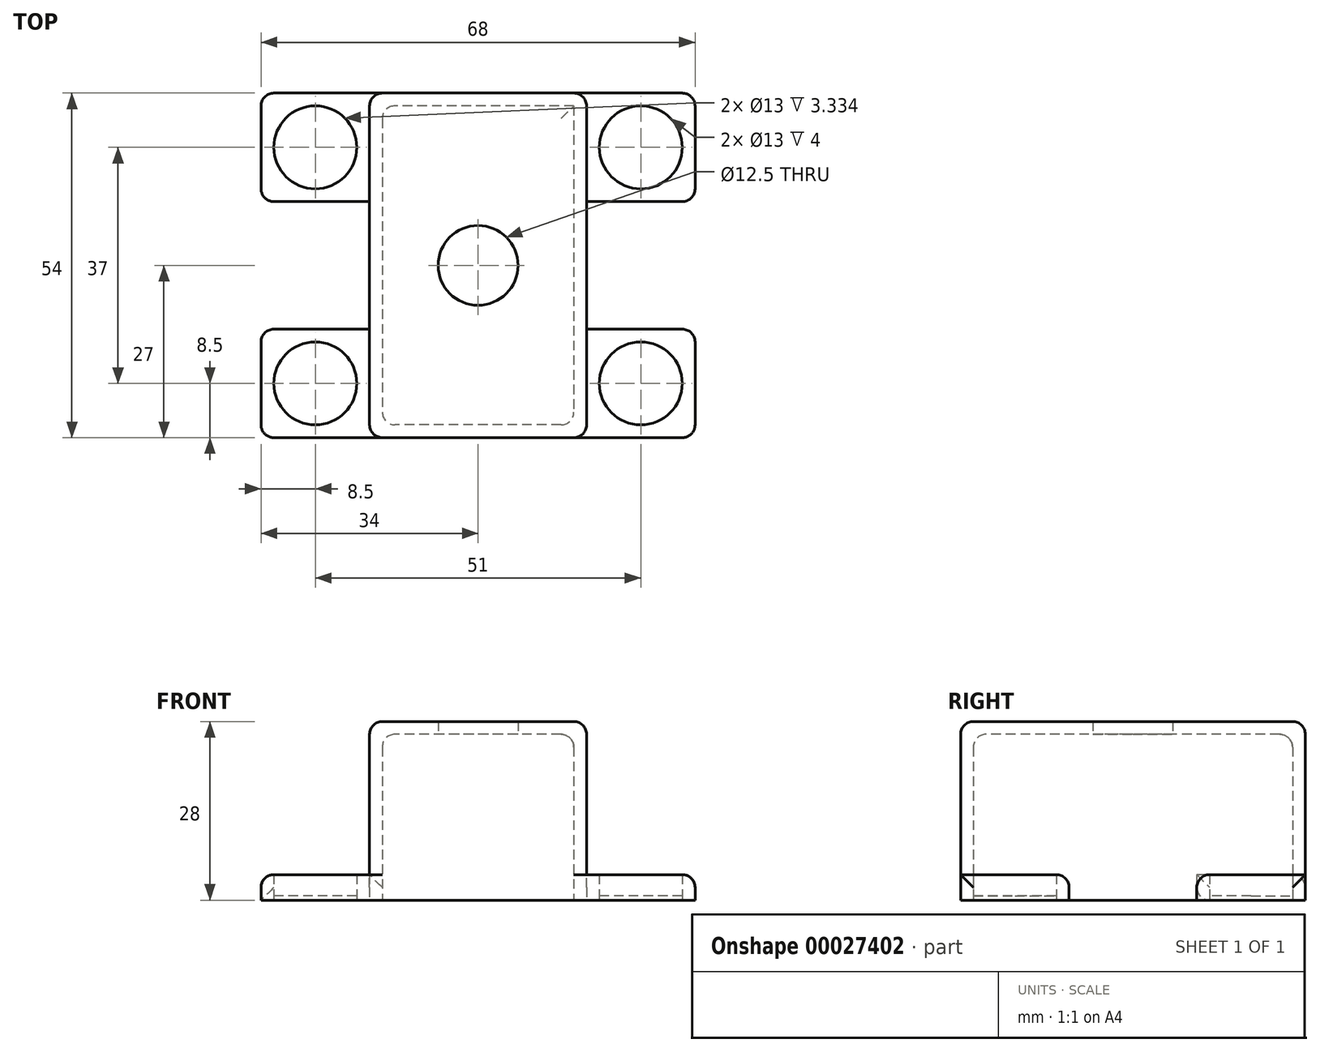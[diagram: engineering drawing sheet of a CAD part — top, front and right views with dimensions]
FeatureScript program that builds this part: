
annotation { "Feature Type Name" : "Feature", "Feature Type Description" : "" }
export const myFeature = defineFeature(function(context is Context, id is Id, definition is map)
    precondition{}
    {
        {
            var Q0;
            Q0=qCreatedBy(makeId("Top.planeOp"),FACE);
            var sketch = newSketch(context, id + "F0", { "sketchPlane" : qUnion([Q0])});
            skLineSegment(sketch, "E0.rect.bottom", {"start": v(17, 27) * mm, "end": v(-17, 27) * mm});
            skLineSegment(sketch, "E0.rect.top", {"start": v(17, -27) * mm, "end": v(-17, -27) * mm});
            skLineSegment(sketch, "E0.rect.left", {"start": v(17, 27) * mm, "end": v(17, -27) * mm});
            skLineSegment(sketch, "E0.rect.right", {"start": v(-17, 27) * mm, "end": v(-17, -27) * mm});
            skPoint(sketch, "E0.rect.middle", {"position": v(0, 0) * mm});
            skLineSegment(sketch, "E1", {"start": v(0, -27) * mm, "end": v(0, 27) * mm, "construction": true});
            skCircle(sketch, "E2", {"center": v(0, 0) * mm, "radius": 6.25 * mm});
            skLineSegment(sketch, "E3.0", {"start": v(-15, 25) * mm, "end": v(-15, -25) * mm});
            skLineSegment(sketch, "E3.1", {"start": v(15, 25) * mm, "end": v(-15, 25) * mm});
            skLineSegment(sketch, "E3.2", {"start": v(15, 25) * mm, "end": v(15, -25) * mm});
            skLineSegment(sketch, "E3.3", {"start": v(15, -25) * mm, "end": v(-15, -25) * mm});
            skCircle(sketch, "E4", {"center": v(-25.5, 18.5) * mm, "radius": 6.5 * mm});
            skLineSegment(sketch, "E5", {"start": v(-17, 27) * mm, "end": v(-34, 27) * mm});
            skLineSegment(sketch, "E6", {"start": v(-34, 27) * mm, "end": v(-34, 10) * mm});
            skLineSegment(sketch, "E7", {"start": v(-34, 10) * mm, "end": v(-17, 10) * mm});
            skLineSegment(sketch, "E8.MirrorCS", {"start": v(34, 10) * mm, "end": v(17, 10) * mm});
            skCircle(sketch, "E9.MirrorC", {"center": v(25.5, 18.5) * mm, "radius": 6.5 * mm});
            skLineSegment(sketch, "E10.MirrorCS", {"start": v(34, 27) * mm, "end": v(34, 10) * mm});
            skLineSegment(sketch, "E11.MirrorCS", {"start": v(17, 27) * mm, "end": v(34, 27) * mm});
            skLineSegment(sketch, "E12", {"start": v(-17, 0) * mm, "end": v(17, 0) * mm, "construction": true});
            skCircle(sketch, "E13.MirrorC", {"center": v(25.5, -18.5) * mm, "radius": 6.5 * mm});
            skLineSegment(sketch, "E14.MirrorCS", {"start": v(34, -27) * mm, "end": v(34, -10) * mm});
            skLineSegment(sketch, "E15.MirrorCS", {"start": v(17, -27) * mm, "end": v(34, -27) * mm});
            skLineSegment(sketch, "E16.MirrorCS", {"start": v(34, -10) * mm, "end": v(17, -10) * mm});
            skLineSegment(sketch, "E17.MirrorCS", {"start": v(-34, -10) * mm, "end": v(-17, -10) * mm});
            skLineSegment(sketch, "E18.MirrorCS", {"start": v(-34, -27) * mm, "end": v(-34, -10) * mm});
            skLineSegment(sketch, "E19.MirrorCS", {"start": v(-17, -27) * mm, "end": v(-34, -27) * mm});
            skCircle(sketch, "E20.MirrorC", {"center": v(-25.5, -18.5) * mm, "radius": 6.5 * mm});
            skSolve(sketch);
        }
        {
            var Q0;
            {var subQ4=sQuery(id+"F0.wireOp",EDGE,"E0.rect.bottom");Q0=makeQuery(id+"F0.imprint","IMPRINT",FACE,{"disambiguationData":[TD([[makeQuery(id+"F0.imprint","IMPRINT",EDGE,{"derivedFrom":subQ4}),1.0]])]});}
            var Q1;
            Q1=makeQuery(id+"F0.imprint","IMPRINT",FACE,{"disambiguationData":[TD([[makeQuery(id+"F0.imprint","IMPRINT",EDGE,{"derivedFrom":sQuery(id+"F0.wireOp",EDGE,"E2")}),1.0]])]});
            var Q2;
            Q2=makeQuery(id+"F0.imprint","IMPRINT",FACE,{"disambiguationData":[TD([[makeQuery(id+"F0.imprint","IMPRINT",EDGE,{"derivedFrom":sQuery(id+"F0.wireOp",EDGE,"E2")}),-1.0]])]});
            extrude(context, id + "F1", {"entities" : qUnion([Q0, Q1, Q2]), "depth" : 28 * mm});
        }
        {
            var Q0;
            Q0=makeQuery(id+"F0.imprint","IMPRINT",FACE,{"disambiguationData":[TD([[makeQuery(id+"F0.imprint","IMPRINT",EDGE,{"derivedFrom":sQuery(id+"F0.wireOp",EDGE,"E2")}),1.0]])]});
            extrude(context, id + "F2", {"entities" : qUnion([Q0]), "operationType" : NewBodyOperationType.REMOVE, "endBound" : BoundingType.THROUGH_ALL, "depth" : 25 * mm});
        }
        {
            var Q0;
            Q0=makeQuery(id+"F0.imprint","IMPRINT",FACE,{"disambiguationData":[TD([[makeQuery(id+"F0.imprint","IMPRINT",EDGE,{"derivedFrom":sQuery(id+"F0.wireOp",EDGE,"E2")}),-1.0]])]});
            extrude(context, id + "F3", {"entities" : qUnion([Q0]), "operationType" : NewBodyOperationType.REMOVE, "depth" : 26 * mm});
        }
        {
            var Q0;
            Q0=makeQuery(id+"F0.imprint","IMPRINT",FACE,{"disambiguationData":[TD([[makeQuery(id+"F0.imprint","IMPRINT",EDGE,{"derivedFrom":sQuery(id+"F0.wireOp",EDGE,"E4")}),-1.0]])]});
            var Q1;
            {var subQ1=sQuery(id+"F0.wireOp",EDGE,"E8.MirrorCS");Q1=makeQuery(id+"F0.imprint","IMPRINT",FACE,{"disambiguationData":[TD([[makeQuery(id+"F0.imprint","IMPRINT",EDGE,{"derivedFrom":subQ1}),-1.0]])]});}
            var Q2;
            Q2=makeQuery(id+"F0.imprint","IMPRINT",FACE,{"disambiguationData":[TD([[makeQuery(id+"F0.imprint","IMPRINT",EDGE,{"derivedFrom":sQuery(id+"F0.wireOp",EDGE,"E13.MirrorC")}),-1.0]])]});
            var Q3;
            {var subQ1=sQuery(id+"F0.wireOp",EDGE,"E17.MirrorCS");Q3=makeQuery(id+"F0.imprint","IMPRINT",FACE,{"disambiguationData":[TD([[makeQuery(id+"F0.imprint","IMPRINT",EDGE,{"derivedFrom":subQ1}),-1.0]])]});}
            extrude(context, id + "F4", {"entities" : qUnion([Q0, Q1, Q2, Q3]), "operationType" : NewBodyOperationType.ADD, "depth" : 4 * mm});
        }
        {
            var Q0;
            Q0=makeQuery(id+"F0.imprint","IMPRINT",FACE,{"disambiguationData":[TD([[makeQuery(id+"F0.imprint","IMPRINT",EDGE,{"derivedFrom":sQuery(id+"F0.wireOp",EDGE,"E9.MirrorC")}),-1.0]])]});
            var Q1;
            Q1=makeQuery(id+"F0.imprint","IMPRINT",FACE,{"disambiguationData":[TD([[makeQuery(id+"F0.imprint","IMPRINT",EDGE,{"derivedFrom":sQuery(id+"F0.wireOp",EDGE,"E13.MirrorC")}),1.0]])]});
            var Q2;
            Q2=makeQuery(id+"F0.imprint","IMPRINT",FACE,{"disambiguationData":[TD([[makeQuery(id+"F0.imprint","IMPRINT",EDGE,{"derivedFrom":sQuery(id+"F0.wireOp",EDGE,"E20.MirrorC")}),-1.0]])]});
            var Q3;
            Q3=makeQuery(id+"F0.imprint","IMPRINT",FACE,{"disambiguationData":[TD([[makeQuery(id+"F0.imprint","IMPRINT",EDGE,{"derivedFrom":sQuery(id+"F0.wireOp",EDGE,"E4")}),1.0]])]});
            extrude(context, id + "F5", {"entities" : qUnion([Q0, Q1, Q2, Q3]), "operationType" : NewBodyOperationType.ADD, "depth" : .666 * mm});
        }
        {
            var Q0;
            Q0=makeQuery(id+"F4.opExtrude","SWEPT_EDGE",EDGE,{"disambiguationData":[OSD([sQuery(id+"F0.wireOp",EDGE,"E18.MirrorCS"),sQuery(id+"F0.wireOp",EDGE,"E19.MirrorCS")])]});
            var Q1;
            Q1=makeQuery(id+"F4.opExtrude","SWEPT_EDGE",EDGE,{"disambiguationData":[OSD([sQuery(id+"F0.wireOp",EDGE,"E17.MirrorCS"),sQuery(id+"F0.wireOp",EDGE,"E18.MirrorCS")])]});
            var Q2;
            {var subQ0=sQuery(id+"F0.wireOp",EDGE,"E0.rect.right");Q2=makeQuery(id+"F4.opExtrude","CAP_EDGE",EDGE,{"disambiguationData":[OSD([subQ0]),TDD([makeQuery(id+"F0.imprint","IMPRINT",EDGE,{"disambiguationData":[TD([[makeQuery(id+"F0.imprint","INTERSECT",VERTEX,{"derivedFrom":[subQ0,sQuery(id+"F0.wireOp",EDGE,"E17.MirrorCS")]}),-1.0]])],"derivedFrom":subQ0})])],"isStart":false});}
            var Q3;
            Q3=makeQuery(id+"F4.opExtrude","SWEPT_EDGE",EDGE,{"disambiguationData":[OSD([sQuery(id+"F0.wireOp",EDGE,"E0.rect.right"),sQuery(id+"F0.wireOp",EDGE,"E17.MirrorCS")])]});
            var Q4;
            Q4=makeQuery(id+"F4.opExtrude","SWEPT_EDGE",EDGE,{"disambiguationData":[OSD([sQuery(id+"F0.wireOp",EDGE,"E0.rect.right"),sQuery(id+"F0.wireOp",EDGE,"E7")])]});
            var Q5;
            Q5=makeQuery(id+"F4.opExtrude","SWEPT_EDGE",EDGE,{"disambiguationData":[OSD([sQuery(id+"F0.wireOp",EDGE,"E6"),sQuery(id+"F0.wireOp",EDGE,"E7")])]});
            var Q6;
            Q6=makeQuery(id+"F4.opExtrude","SWEPT_EDGE",EDGE,{"disambiguationData":[OSD([sQuery(id+"F0.wireOp",EDGE,"E5"),sQuery(id+"F0.wireOp",EDGE,"E6")])]});
            var Q7;
            {var subQ0=sQuery(id+"F0.wireOp",EDGE,"E0.rect.right");Q7=makeQuery(id+"F4.opExtrude","CAP_EDGE",EDGE,{"disambiguationData":[OSD([subQ0]),TDD([makeQuery(id+"F0.imprint","IMPRINT",EDGE,{"disambiguationData":[TD([[makeQuery(id+"F0.imprint","INTERSECT",VERTEX,{"derivedFrom":[subQ0,sQuery(id+"F0.wireOp",EDGE,"E7")]}),1.0]])],"derivedFrom":subQ0})])],"isStart":false});}
            var Q8;
            Q8=makeQuery(id+"F4.opExtrude","SWEPT_EDGE",EDGE,{"disambiguationData":[OSD([sQuery(id+"F0.wireOp",EDGE,"E0.rect.left"),sQuery(id+"F0.wireOp",EDGE,"E8.MirrorCS")])]});
            var Q9;
            {var subQ0=sQuery(id+"F0.wireOp",EDGE,"E0.rect.left");Q9=makeQuery(id+"F4.opExtrude","CAP_EDGE",EDGE,{"disambiguationData":[OSD([subQ0]),TDD([makeQuery(id+"F0.imprint","IMPRINT",EDGE,{"disambiguationData":[TD([[makeQuery(id+"F0.imprint","INTERSECT",VERTEX,{"derivedFrom":[subQ0,sQuery(id+"F0.wireOp",EDGE,"E8.MirrorCS")]}),1.0]])],"derivedFrom":subQ0})])],"isStart":false});}
            var Q10;
            Q10=makeQuery(id+"F4.opExtrude","SWEPT_EDGE",EDGE,{"disambiguationData":[OSD([sQuery(id+"F0.wireOp",EDGE,"E8.MirrorCS"),sQuery(id+"F0.wireOp",EDGE,"E10.MirrorCS")])]});
            var Q11;
            Q11=makeQuery(id+"F4.opExtrude","SWEPT_EDGE",EDGE,{"disambiguationData":[OSD([sQuery(id+"F0.wireOp",EDGE,"E10.MirrorCS"),sQuery(id+"F0.wireOp",EDGE,"E11.MirrorCS")])]});
            var Q12;
            Q12=makeQuery(id+"F4.opExtrude","SWEPT_EDGE",EDGE,{"disambiguationData":[OSD([sQuery(id+"F0.wireOp",EDGE,"E14.MirrorCS"),sQuery(id+"F0.wireOp",EDGE,"E16.MirrorCS")])]});
            var Q13;
            {var subQ0=sQuery(id+"F0.wireOp",EDGE,"E0.rect.left");Q13=makeQuery(id+"F4.opExtrude","CAP_EDGE",EDGE,{"disambiguationData":[OSD([subQ0]),TDD([makeQuery(id+"F0.imprint","IMPRINT",EDGE,{"disambiguationData":[TD([[makeQuery(id+"F0.imprint","INTERSECT",VERTEX,{"derivedFrom":[subQ0,sQuery(id+"F0.wireOp",EDGE,"E16.MirrorCS")]}),-1.0]])],"derivedFrom":subQ0})])],"isStart":false});}
            var Q14;
            Q14=makeQuery(id+"F4.opExtrude","SWEPT_EDGE",EDGE,{"disambiguationData":[OSD([sQuery(id+"F0.wireOp",EDGE,"E14.MirrorCS"),sQuery(id+"F0.wireOp",EDGE,"E15.MirrorCS")])]});
            var Q15;
            Q15=makeQuery(id+"F4.opExtrude","SWEPT_EDGE",EDGE,{"disambiguationData":[OSD([sQuery(id+"F0.wireOp",EDGE,"E0.rect.left"),sQuery(id+"F0.wireOp",EDGE,"E16.MirrorCS")])]});
            var Q16;
            Q16=makeQuery(id+"F1.opExtrude","SWEPT_EDGE",EDGE,{"disambiguationData":[OSD([sQuery(id+"F0.wireOp",EDGE,"E0.rect.bottom"),sQuery(id+"F0.wireOp",EDGE,"E0.rect.left"),sQuery(id+"F0.wireOp",EDGE,"E11.MirrorCS")])]});
            var Q17;
            Q17=makeQuery(id+"F4.opExtrude","CAP_EDGE",EDGE,{"disambiguationData":[OSD([sQuery(id+"F0.wireOp",EDGE,"E10.MirrorCS")])],"isStart":false});
            var Q18;
            Q18=makeQuery(id+"F4.opExtrude","CAP_EDGE",EDGE,{"disambiguationData":[OSD([sQuery(id+"F0.wireOp",EDGE,"E8.MirrorCS")])],"isStart":false});
            var Q19;
            Q19=makeQuery(id+"F1.opExtrude","SWEPT_EDGE",EDGE,{"disambiguationData":[OSD([sQuery(id+"F0.wireOp",EDGE,"E0.rect.bottom"),sQuery(id+"F0.wireOp",EDGE,"E0.rect.right"),sQuery(id+"F0.wireOp",EDGE,"E5")])]});
            var Q20;
            Q20=makeQuery(id+"F4.opExtrude","CAP_EDGE",EDGE,{"disambiguationData":[OSD([sQuery(id+"F0.wireOp",EDGE,"E5")])],"isStart":false});
            var Q21;
            Q21=makeQuery(id+"F4.opExtrude","CAP_EDGE",EDGE,{"disambiguationData":[OSD([sQuery(id+"F0.wireOp",EDGE,"E6")])],"isStart":false});
            var Q22;
            Q22=makeQuery(id+"F4.opExtrude","CAP_EDGE",EDGE,{"disambiguationData":[OSD([sQuery(id+"F0.wireOp",EDGE,"E7")])],"isStart":true});
            var Q23;
            Q23=makeQuery(id+"F1.opExtrude","SWEPT_EDGE",EDGE,{"disambiguationData":[OSD([sQuery(id+"F0.wireOp",EDGE,"E0.rect.top"),sQuery(id+"F0.wireOp",EDGE,"E0.rect.right"),sQuery(id+"F0.wireOp",EDGE,"E19.MirrorCS")])]});
            var Q24;
            Q24=makeQuery(id+"F4.opExtrude","CAP_EDGE",EDGE,{"disambiguationData":[OSD([sQuery(id+"F0.wireOp",EDGE,"E18.MirrorCS")])],"isStart":false});
            var Q25;
            Q25=makeQuery(id+"F4.opExtrude","CAP_EDGE",EDGE,{"disambiguationData":[OSD([sQuery(id+"F0.wireOp",EDGE,"E17.MirrorCS")])],"isStart":false});
            var Q26;
            Q26=makeQuery(id+"F1.opExtrude","SWEPT_EDGE",EDGE,{"disambiguationData":[OSD([sQuery(id+"F0.wireOp",EDGE,"E0.rect.top"),sQuery(id+"F0.wireOp",EDGE,"E0.rect.left"),sQuery(id+"F0.wireOp",EDGE,"E15.MirrorCS")])]});
            var Q27;
            Q27=makeQuery(id+"F4.opExtrude","CAP_EDGE",EDGE,{"disambiguationData":[OSD([sQuery(id+"F0.wireOp",EDGE,"E14.MirrorCS")])],"isStart":false});
            var Q28;
            Q28=makeQuery(id+"F4.opExtrude","CAP_EDGE",EDGE,{"disambiguationData":[OSD([sQuery(id+"F0.wireOp",EDGE,"E16.MirrorCS")])],"isStart":false});
            var Q29;
            Q29=makeQuery(id+"F1.opExtrude","CAP_EDGE",EDGE,{"disambiguationData":[OSD([sQuery(id+"F0.wireOp",EDGE,"E0.rect.left")])],"isStart":false});
            var Q30;
            Q30=makeQuery(id+"F1.opExtrude","CAP_EDGE",EDGE,{"disambiguationData":[OSD([sQuery(id+"F0.wireOp",EDGE,"E0.rect.right")])],"isStart":false});
            var Q31;
            Q31=makeQuery(id+"F1.opExtrude","CAP_EDGE",EDGE,{"disambiguationData":[OSD([sQuery(id+"F0.wireOp",EDGE,"E0.rect.bottom")])],"isStart":false});
            var Q32;
            Q32=makeQuery(id+"F1.opExtrude","CAP_EDGE",EDGE,{"disambiguationData":[OSD([sQuery(id+"F0.wireOp",EDGE,"E0.rect.top")])],"isStart":false});
            var Q33;
            Q33=makeQuery(id+"F3.boolean.opBoolean","COPY",EDGE,{"derivedFrom":makeQuery(id+"F3.opExtrude","CAP_EDGE",EDGE,{"disambiguationData":[OSD([sQuery(id+"F0.wireOp",EDGE,"E3.3")])],"isStart":false})});
            var Q34;
            Q34=makeQuery(id+"F3.boolean.opBoolean","COPY",EDGE,{"derivedFrom":makeQuery(id+"F3.opExtrude","CAP_EDGE",EDGE,{"disambiguationData":[OSD([sQuery(id+"F0.wireOp",EDGE,"E3.2")])],"isStart":false})});
            var Q35;
            Q35=makeQuery(id+"F3.boolean.opBoolean","COPY",EDGE,{"derivedFrom":makeQuery(id+"F3.opExtrude","SWEPT_EDGE",EDGE,{"disambiguationData":[OSD([sQuery(id+"F0.wireOp",EDGE,"E3.2"),sQuery(id+"F0.wireOp",EDGE,"E3.3")])]})});
            var Q36;
            Q36=makeQuery(id+"F3.boolean.opBoolean","COPY",EDGE,{"derivedFrom":makeQuery(id+"F3.opExtrude","SWEPT_EDGE",EDGE,{"disambiguationData":[OSD([sQuery(id+"F0.wireOp",EDGE,"E3.0"),sQuery(id+"F0.wireOp",EDGE,"E3.3")])]})});
            var Q37;
            Q37=makeQuery(id+"F3.boolean.opBoolean","COPY",EDGE,{"derivedFrom":makeQuery(id+"F3.opExtrude","CAP_EDGE",EDGE,{"disambiguationData":[OSD([sQuery(id+"F0.wireOp",EDGE,"E3.0")])],"isStart":false})});
            var Q38;
            Q38=makeQuery(id+"F3.boolean.opBoolean","COPY",EDGE,{"derivedFrom":makeQuery(id+"F3.opExtrude","CAP_EDGE",EDGE,{"disambiguationData":[OSD([sQuery(id+"F0.wireOp",EDGE,"E3.1")])],"isStart":false})});
            var Q39;
            Q39=makeQuery(id+"F3.boolean.opBoolean","COPY",EDGE,{"derivedFrom":makeQuery(id+"F3.opExtrude","SWEPT_EDGE",EDGE,{"disambiguationData":[OSD([sQuery(id+"F0.wireOp",EDGE,"E3.0"),sQuery(id+"F0.wireOp",EDGE,"E3.1")])]})});
            fillet(context, id + "F6", {"entities" : qUnion([Q0, Q1, Q2, Q3, Q4, Q5, Q6, Q7, Q8, Q9, Q10, Q11, Q12, Q13, Q14, Q15, Q16, Q17, Q18, Q19, Q20, Q21, Q22, Q23, Q24, Q25, Q26, Q27, Q28, Q29, Q30, Q31, Q32, Q33, Q34, Q35, Q36, Q37, Q38, Q39]), "radius" : 2 * mm, "tangentPropagation" : true, "allowEdgeOverflow" : false});
        }
    });
